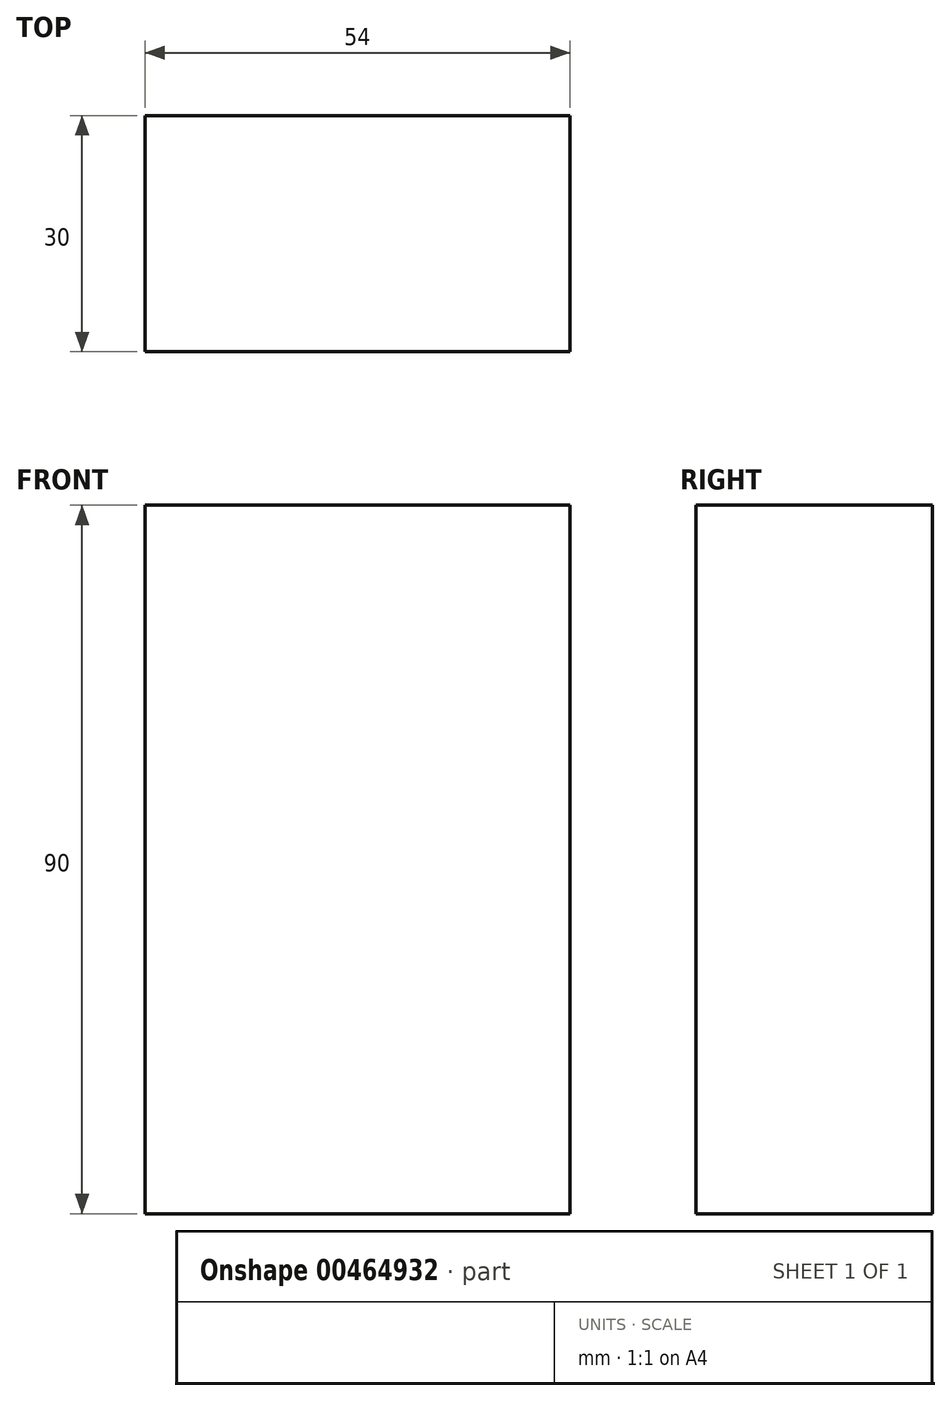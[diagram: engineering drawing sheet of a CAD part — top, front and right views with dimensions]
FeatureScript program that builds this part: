
annotation { "Feature Type Name" : "Feature", "Feature Type Description" : "" }
export const myFeature = defineFeature(function(context is Context, id is Id, definition is map)
    precondition{}
    {
        {
            var Q0;
            Q0=qCreatedBy(makeId("Right.planeOp"),FACE);
            var sketch = newSketch(context, id + "F0", { "sketchPlane" : qUnion([Q0])});
            skLineSegment(sketch, "E0.bottom", {"start": v(-15, 45) * mm, "end": v(15, 45) * mm});
            skLineSegment(sketch, "E0.top", {"start": v(-15, -45) * mm, "end": v(15, -45) * mm});
            skLineSegment(sketch, "E0.left", {"start": v(-15, 45) * mm, "end": v(-15, -45) * mm});
            skLineSegment(sketch, "E0.right", {"start": v(15, 45) * mm, "end": v(15, -45) * mm});
            skPoint(sketch, "E0.middle", {"position": v(0, 0) * mm});
            skSolve(sketch);
        }
        {
            var Q0;
            Q0=makeQuery(id+"F0.imprint","IMPRINT",FACE,{"disambiguationData":[TD([[makeQuery(id+"F0.imprint","IMPRINT",EDGE,{"derivedFrom":sQuery(id+"F0.wireOp",EDGE,"E0.bottom")}),-1.0]])]});
            extrude(context, id + "F1", {"entities" : qUnion([Q0]), "endBound" : BoundingType.SYMMETRIC, "depth" : 54 * mm, "offsetDistance" : 25 * mm});
        }
    });
